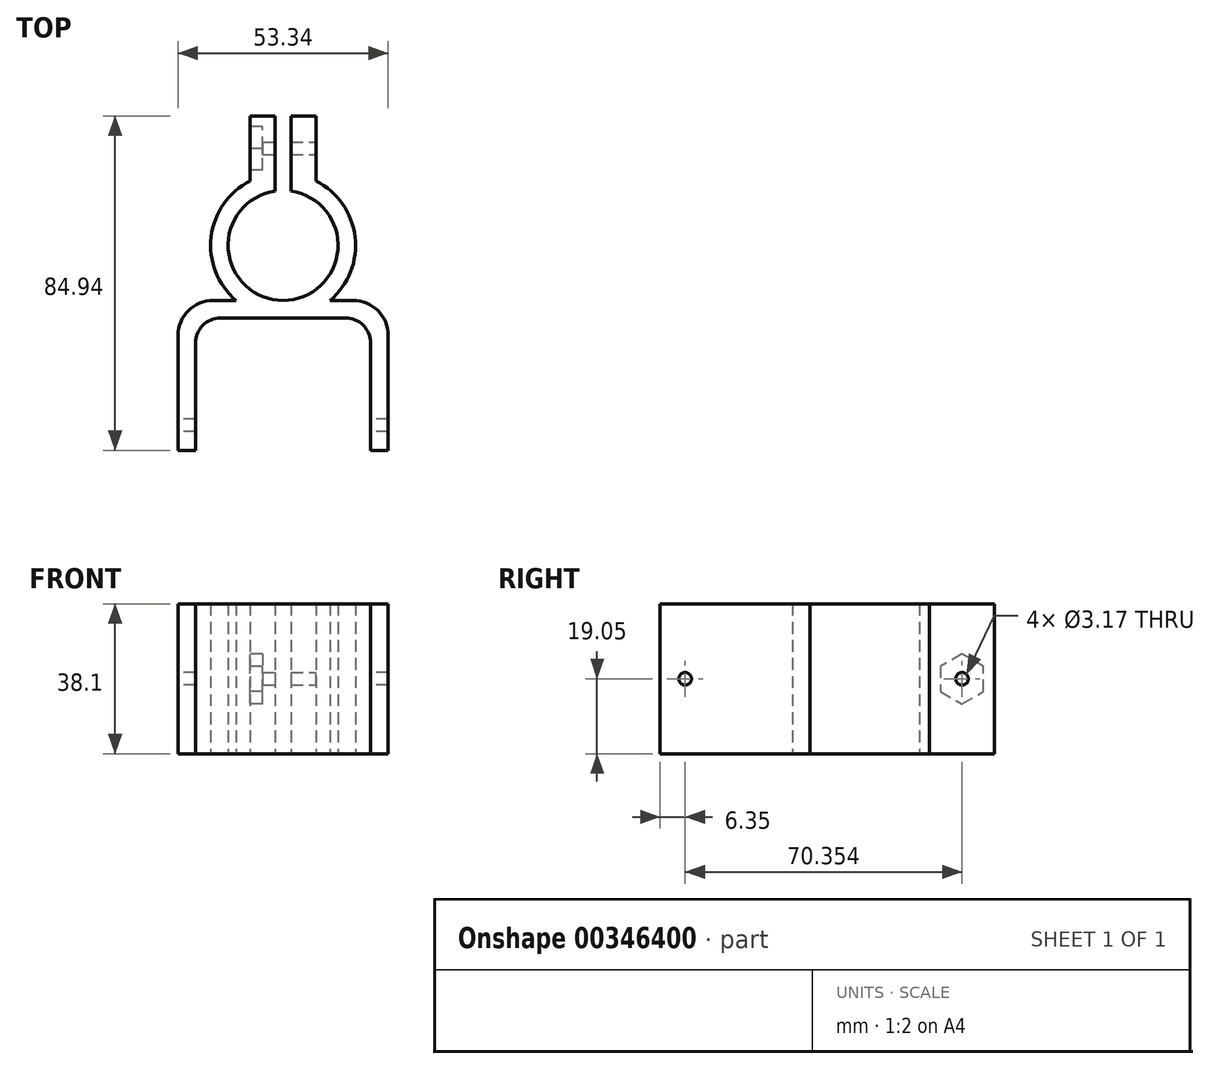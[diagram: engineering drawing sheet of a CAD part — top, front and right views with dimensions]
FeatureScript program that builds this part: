
annotation { "Feature Type Name" : "Feature", "Feature Type Description" : "" }
export const myFeature = defineFeature(function(context is Context, id is Id, definition is map)
    precondition{}
    {
        {
            var Q0;
            Q0=qCreatedBy(makeId("Top.planeOp"),FACE);
            var sketch = newSketch(context, id + "F0", { "sketchPlane" : qUnion([Q0])});
            skLineSegment(sketch, "E0.bottom", {"start": v(-17.78, 0) * mm, "end": v(17.78, 0) * mm});
            skLineSegment(sketch, "E0.top", {"start": v(-26.67, -38.1) * mm, "end": v(26.67, -38.1) * mm});
            skLineSegment(sketch, "E0.left", {"start": v(-26.67, -8.89) * mm, "end": v(-26.67, -38.1) * mm});
            skLineSegment(sketch, "E0.right", {"start": v(26.67, -8.9) * mm, "end": v(26.67, -38.1) * mm});
            skLineSegment(sketch, "E1.0", {"start": v(-22.23, -10.8) * mm, "end": v(-22.23, -38.1) * mm});
            skLineSegment(sketch, "E1.1", {"start": v(-15.87, -4.45) * mm, "end": v(15.87, -4.45) * mm});
            skLineSegment(sketch, "E1.2", {"start": v(22.23, -10.8) * mm, "end": v(22.23, -38.1) * mm});
            skCircle(sketch, "E2", {"center": v(0, 13.97) * mm, "radius": 13.97 * mm});
            skCircle(sketch, "E3.0", {"center": v(0, 13.97) * mm, "radius": 18.42 * mm});
            skLineSegment(sketch, "E4.bottom", {"start": v(-2.03, 27.8) * mm, "end": v(-8.38, 27.8) * mm});
            skLineSegment(sketch, "E4.top", {"start": v(-2.03, 46.84) * mm, "end": v(-8.38, 46.84) * mm});
            skLineSegment(sketch, "E4.left", {"start": v(-2.03, 27.8) * mm, "end": v(-2.03, 46.84) * mm});
            skLineSegment(sketch, "E4.right", {"start": v(-8.38, 27.8) * mm, "end": v(-8.38, 46.84) * mm});
            skLineSegment(sketch, "E5.MirrorCS", {"start": v(2.03, 27.8) * mm, "end": v(2.03, 46.84) * mm});
            skLineSegment(sketch, "E6.MirrorCS", {"start": v(2.03, 27.8) * mm, "end": v(8.38, 27.8) * mm});
            skLineSegment(sketch, "E7.MirrorCS", {"start": v(8.38, 27.8) * mm, "end": v(8.38, 46.84) * mm});
            skLineSegment(sketch, "E8.MirrorCS", {"start": v(2.03, 46.84) * mm, "end": v(8.38, 46.84) * mm});
            skPoint(sketch, "E9.visualSharp", {"position": v(-22.23, -4.44) * mm});
            skArc(sketch, "E9.filletArc", {"start": v(-15.87, -4.45) * mm, "mid": v(-20.37, -6.3) * mm, "end": v(-22.22, -10.8) * mm});
            skPoint(sketch, "E10.visualSharp", {"position": v(22.23, -4.44) * mm});
            skArc(sketch, "E10.filletArc", {"start": v(22.22, -10.8) * mm, "mid": v(20.37, -6.3) * mm, "end": v(15.87, -4.45) * mm});
            skPoint(sketch, "E11.visualSharp", {"position": v(-26.67, 0) * mm});
            skArc(sketch, "E11.filletArc", {"start": v(-17.78, 0) * mm, "mid": v(-24.07, -2.6) * mm, "end": v(-26.67, -8.89) * mm});
            skPoint(sketch, "E12.visualSharp", {"position": v(26.67, 0) * mm});
            skArc(sketch, "E12.filletArc", {"start": v(26.67, -8.9) * mm, "mid": v(24.07, -2.6) * mm, "end": v(17.78, 0) * mm});
            skSolve(sketch);
        }
        {
            var Q0;
            {var subQ0=sQuery(id+"F0.wireOp",EDGE,"E0.left");Q0=makeQuery(id+"F0.imprint","IMPRINT",FACE,{"disambiguationData":[TD([[makeQuery(id+"F0.imprint","IMPRINT",EDGE,{"derivedFrom":subQ0}),1.0]])]});}
            var Q1;
            {var subQ0=sQuery(id+"F0.wireOp",EDGE,"E3.0");var subQ1=sQuery(id+"F0.wireOp",EDGE,"E0.bottom");var subQ2=makeQuery(id+"F0.imprint","INTERSECT",VERTEX,{"disambiguationData":[OD(0.0)],"derivedFrom":[subQ1,subQ0]});Q1=makeQuery(id+"F0.imprint","IMPRINT",FACE,{"disambiguationData":[TD([[makeQuery(id+"F0.imprint","IMPRINT",EDGE,{"disambiguationData":[TD([[subQ2,-1.0]])],"derivedFrom":subQ1}),-1.0]])]});}
            var Q2;
            {var subQ4=sQuery(id+"F0.wireOp",EDGE,"E0.right");Q2=makeQuery(id+"F0.imprint","IMPRINT",FACE,{"disambiguationData":[TD([[makeQuery(id+"F0.imprint","IMPRINT",EDGE,{"derivedFrom":subQ4}),-1.0]])]});}
            var Q3;
            {var subQ0=sQuery(id+"F0.wireOp",EDGE,"E6.MirrorCS");Q3=makeQuery(id+"F0.imprint","IMPRINT",FACE,{"disambiguationData":[TD([[makeQuery(id+"F0.imprint","IMPRINT",EDGE,{"derivedFrom":subQ0}),-1.0]])]});}
            var Q4;
            {var subQ0=sQuery(id+"F0.wireOp",EDGE,"E4.bottom");Q4=makeQuery(id+"F0.imprint","IMPRINT",FACE,{"disambiguationData":[TD([[makeQuery(id+"F0.imprint","IMPRINT",EDGE,{"derivedFrom":subQ0}),1.0]])]});}
            var Q5;
            {var subQ5=sQuery(id+"F0.wireOp",EDGE,"E6.MirrorCS");Q5=makeQuery(id+"F0.imprint","IMPRINT",FACE,{"disambiguationData":[TD([[makeQuery(id+"F0.imprint","IMPRINT",EDGE,{"derivedFrom":subQ5}),1.0]])]});}
            var Q6;
            {var subQ5=sQuery(id+"F0.wireOp",EDGE,"E8.MirrorCS");Q6=makeQuery(id+"F0.imprint","IMPRINT",FACE,{"disambiguationData":[TD([[makeQuery(id+"F0.imprint","IMPRINT",EDGE,{"derivedFrom":subQ5}),-1.0]])]});}
            var Q7;
            {var subQ5=sQuery(id+"F0.wireOp",EDGE,"E4.bottom");Q7=makeQuery(id+"F0.imprint","IMPRINT",FACE,{"disambiguationData":[TD([[makeQuery(id+"F0.imprint","IMPRINT",EDGE,{"derivedFrom":subQ5}),-1.0]])]});}
            var Q8;
            {var subQ5=sQuery(id+"F0.wireOp",EDGE,"E4.top");Q8=makeQuery(id+"F0.imprint","IMPRINT",FACE,{"disambiguationData":[TD([[makeQuery(id+"F0.imprint","IMPRINT",EDGE,{"derivedFrom":subQ5}),1.0]])]});}
            extrude(context, id + "F1", {"entities" : qUnion([Q0, Q1, Q2, Q3, Q4, Q5, Q6, Q7, Q8]), "depth" : 38.1 * mm, "offsetDistance" : 25.4 * mm});
        }
        {
            var Q0;
            Q0=makeQuery(id+"F1.opExtrude","SWEPT_FACE",FACE,{"disambiguationData":[OSD([sQuery(id+"F0.wireOp",EDGE,"E7.MirrorCS")])]});
            var sketch = newSketch(context, id + "F2", { "sketchPlane" : qUnion([Q0])});
            skCircle(sketch, "E13", {"center": v(38.6, 19.05) * mm, "radius": 1.59 * mm});
            skPoint(sketch, "E13.centerSnap0", {"position": v(38.6, 38.1) * mm});
            skPoint(sketch, "E13.centerSnap1", {"position": v(30.37, 19.05) * mm});
            skSolve(sketch);
        }
        {
            var Q0;
            Q0=makeQuery(id+"F2.imprint","IMPRINT",FACE,{"disambiguationData":[TD([[makeQuery(id+"F2.imprint","IMPRINT",EDGE,{"derivedFrom":sQuery(id+"F2.wireOp",EDGE,"E13")}),1.0]])]});
            extrude(context, id + "F3", {"entities" : qUnion([Q0]), "operationType" : NewBodyOperationType.REMOVE, "endBound" : BoundingType.THROUGH_ALL, "oppositeDirection" : true, "depth" : 25.4 * mm, "offsetDistance" : 25.4 * mm});
        }
        {
            var Q0;
            Q0=makeQuery(id+"F1.opExtrude","SWEPT_FACE",FACE,{"disambiguationData":[OSD([sQuery(id+"F0.wireOp",EDGE,"E4.right")])]});
            var sketch = newSketch(context, id + "F4", { "sketchPlane" : qUnion([Q0])});
            skCircle(sketch, "E14.cCircle", {"center": v(-38.6, 19.05) * mm, "radius": 5.5 * mm, "construction": true});
            skLineSegment(sketch, "E14.0", {"start": v(-44.1, 15.88) * mm, "end": v(-44.1, 22.23) * mm});
            skLineSegment(sketch, "E14.1", {"start": v(-44.1, 22.23) * mm, "end": v(-38.6, 25.4) * mm});
            skLineSegment(sketch, "E14.2", {"start": v(-38.6, 25.4) * mm, "end": v(-33.1, 22.23) * mm});
            skLineSegment(sketch, "E14.3", {"start": v(-33.1, 22.23) * mm, "end": v(-33.1, 15.88) * mm});
            skLineSegment(sketch, "E14.4", {"start": v(-33.1, 15.88) * mm, "end": v(-38.6, 12.7) * mm});
            skLineSegment(sketch, "E14.5", {"start": v(-38.6, 12.7) * mm, "end": v(-44.1, 15.88) * mm});
            skPoint(sketch, "E14.0.midPoint", {"position": v(-44.1, 19.05) * mm});
            skSolve(sketch);
        }
        {
            var Q0;
            Q0=makeQuery(id+"F4.imprint","IMPRINT",FACE,{"disambiguationData":[TD([[makeQuery(id+"F4.imprint","IMPRINT",EDGE,{"derivedFrom":sQuery(id+"F4.wireOp",EDGE,"E14.0")}),-1.0]])]});
            extrude(context, id + "F5", {"entities" : qUnion([Q0]), "operationType" : NewBodyOperationType.REMOVE, "oppositeDirection" : true, "depth" : 3.17 * mm, "offsetDistance" : 25.4 * mm});
        }
        {
            var Q0;
            Q0=makeQuery(id+"F1.opExtrude","SWEPT_FACE",FACE,{"disambiguationData":[OSD([sQuery(id+"F0.wireOp",EDGE,"E0.left")])]});
            var sketch = newSketch(context, id + "F6", { "sketchPlane" : qUnion([Q0])});
            skCircle(sketch, "E15", {"center": v(31.75, 19.05) * mm, "radius": 1.59 * mm});
            skPoint(sketch, "E15.centerSnap0", {"position": v(38.1, 19.05) * mm});
            skSolve(sketch);
        }
        {
            var Q0;
            Q0=makeQuery(id+"F6.imprint","IMPRINT",FACE,{"disambiguationData":[TD([[makeQuery(id+"F6.imprint","IMPRINT",EDGE,{"derivedFrom":sQuery(id+"F6.wireOp",EDGE,"E15")}),1.0]])]});
            extrude(context, id + "F7", {"entities" : qUnion([Q0]), "operationType" : NewBodyOperationType.REMOVE, "endBound" : BoundingType.THROUGH_ALL, "oppositeDirection" : true, "depth" : 25.4 * mm, "offsetDistance" : 25.4 * mm});
        }
    });
